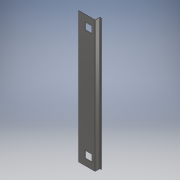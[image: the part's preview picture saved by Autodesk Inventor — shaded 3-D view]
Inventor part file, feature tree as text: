
AUTODESK INVENTOR PART (.ipt)
format: ipt  version: 2017 (Build 210142000, 142)  size: 176,640 bytes
history: native  units: mm
features: sheet_metal_op x6, sketch x3, other x3, extrude x1
ambient origin geometry x8: Origin, YZ Plane, XZ Plane, XY Plane, X Axis, Y Axis, Z Axis, Center Point
bodies: Solid1 (feature_tree)
feature tree (13):
  sheet_metal_op  "Contour Flange1"
  sheet_metal_op  "Flange1"
  extrude  "Extrusion1"  Depth=30.0mm
  sketch  "Sketch1"  dims[d0=100.0mm d1=30.0mm]
  other  "Plate1"
  sheet_metal_op  "Bend1"
  sheet_metal_op  "Corner1"
  sketch  "Sketch2"  dims[d2=1.5mm]
  other  "Plate2"
  sheet_metal_op  "Bend2"
  sheet_metal_op  "Corner2"
  sketch  "Sketch3"  dims[d3=0.75mm d4=3.0mm d5=1.5mm d6=788.0mm d7=1.5mm d8=0.5mm d9=6.0mm d10=1.5mm d11=1.5mm d12=1.5mm d13=0.75mm d14=3.0mm d15=1.5mm d16=10.0mm d17=90.0deg d18=1.5mm d19=6.0mm d20=1.5mm d21=1.5mm d24=40.0mm d25=40.0mm d26=60.0mm d27=60.0mm d28=40.0mm d29=40.0mm d30=60.0mm d31=60.0mm d32=1.5mm d33=0.0mm]
  other  "Definition1"
